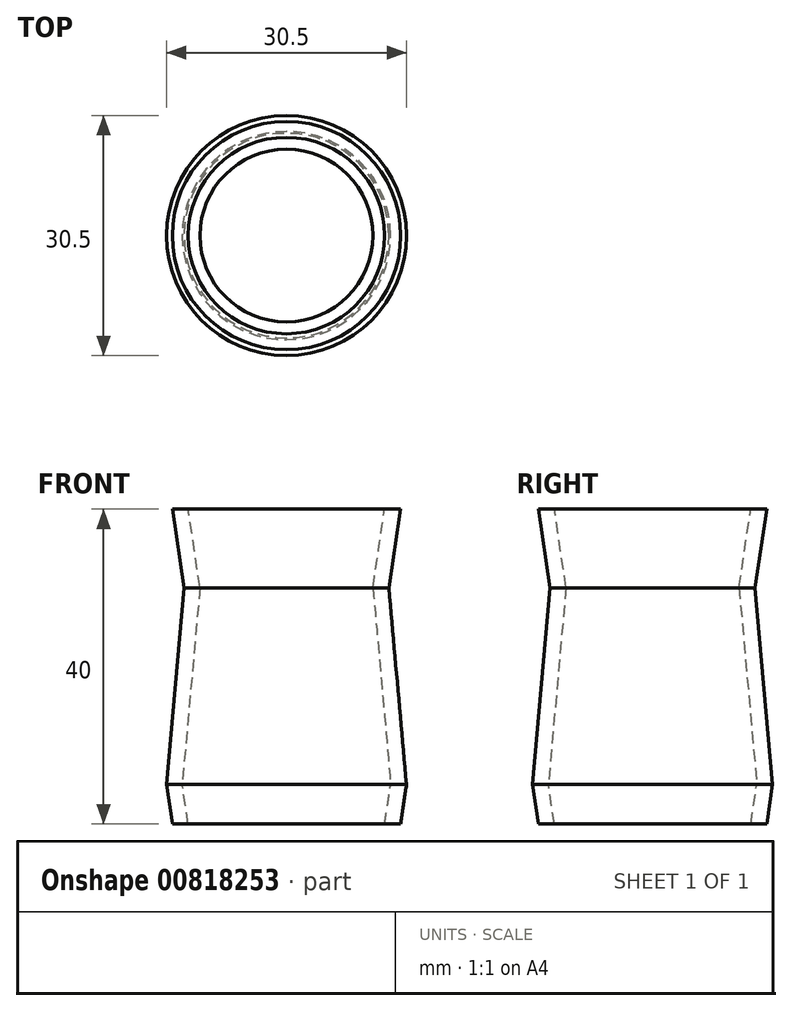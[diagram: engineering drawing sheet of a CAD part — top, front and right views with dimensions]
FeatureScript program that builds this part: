
annotation { "Feature Type Name" : "Feature", "Feature Type Description" : "" }
export const myFeature = defineFeature(function(context is Context, id is Id, definition is map)
    precondition{}
    {
        {
            var Q0;
            Q0=qCreatedBy(makeId("Top.planeOp"),FACE);
            var sketch = newSketch(context, id + "F0", { "sketchPlane" : qUnion([Q0])});
            skCircle(sketch, "E0", {"center": v(0, 0) * mm, "radius": 14.5 * mm});
            skSolve(sketch);
        }
        {
            var Q0;
            Q0=qCreatedBy(makeId("Top.planeOp"),FACE);
            cPlane(context, id + "F1", {"entities" : qUnion([Q0]), "cplaneType" : CPlaneType.OFFSET, "offset" : 5 * mm, "width" : 150 * mm, "height" : 150 * mm});
        }
        {
            var Q0;
            Q0=qCreatedBy(id+"F1.planeOp",FACE);
            var sketch = newSketch(context, id + "F2", { "sketchPlane" : qUnion([Q0])});
            skCircle(sketch, "E1", {"center": v(0, 0) * mm, "radius": 15.25 * mm});
            skSolve(sketch);
        }
        {
            var Q0;
            Q0 = qSketchRegion(id + "F0", true);
            var Q1;
            Q1 = qSketchRegion(id + "F2", true);
            loft(context, id + "F3", {"sheetProfilesArray" : [{ "sheetProfileEntities" : qUnion([Q0]) }, { "sheetProfileEntities" : qUnion([Q1]) }]});
        }
        {
            var Q0;
            Q0=makeQuery(id+"F3.opLoft","CAP_FACE",FACE,{"disambiguationData":[OSD([makeQuery(id+"F2.imprint","IMPRINT",FACE,{"disambiguationData":[TD([[makeQuery(id+"F2.imprint","IMPRINT",EDGE,{"derivedFrom":sQuery(id+"F2.wireOp",EDGE,"E1")}),1.0]])]})])],"isStart":true});
            cPlane(context, id + "F4", {"entities" : qUnion([Q0]), "cplaneType" : CPlaneType.OFFSET, "offset" : 25 * mm, "width" : 150 * mm, "height" : 150 * mm});
        }
        {
            var Q0;
            Q0=qCreatedBy(id+"F4.planeOp",FACE);
            var sketch = newSketch(context, id + "F5", { "sketchPlane" : qUnion([Q0])});
            skCircle(sketch, "E2", {"center": v(0, 0) * mm, "radius": 13 * mm});
            skSolve(sketch);
        }
        {
            var Q1;
            Q1=makeQuery(id+"F3.opLoft","CAP_FACE",FACE,{"disambiguationData":[OSD([makeQuery(id+"F2.imprint","IMPRINT",FACE,{"disambiguationData":[TD([[makeQuery(id+"F2.imprint","IMPRINT",EDGE,{"derivedFrom":sQuery(id+"F2.wireOp",EDGE,"E1")}),1.0]])]})])],"isStart":true});
            var Q2;
            Q2=makeQuery(id+"F5.imprint","IMPRINT",FACE,{"disambiguationData":[TD([[makeQuery(id+"F5.imprint","IMPRINT",EDGE,{"derivedFrom":sQuery(id+"F5.wireOp",EDGE,"E2")}),1.0]])]});
            loft(context, id + "F6", {"operationType" : NewBodyOperationType.ADD, "sheetProfilesArray" : [{ "sheetProfileEntities" : qUnion([Q1]) }, { "sheetProfileEntities" : qUnion([Q2]) }]});
        }
        {
            var Q0;
            Q0=makeQuery(id+"F6.opLoft","CAP_FACE",FACE,{"disambiguationData":[OSD([makeQuery(id+"F5.imprint","IMPRINT",FACE,{"disambiguationData":[TD([[makeQuery(id+"F5.imprint","IMPRINT",EDGE,{"derivedFrom":sQuery(id+"F5.wireOp",EDGE,"E2")}),1.0]])]})])],"isStart":true});
            cPlane(context, id + "F7", {"entities" : qUnion([Q0]), "cplaneType" : CPlaneType.OFFSET, "offset" : 10 * mm, "width" : 150 * mm, "height" : 150 * mm});
        }
        {
            var Q0;
            Q0=qCreatedBy(id+"F7.planeOp",FACE);
            var sketch = newSketch(context, id + "F8", { "sketchPlane" : qUnion([Q0])});
            skCircle(sketch, "E3", {"center": v(0, 0) * mm, "radius": 14.5 * mm});
            skSolve(sketch);
        }
        {
            var Q1;
            Q1=makeQuery(id+"F6.opLoft","CAP_FACE",FACE,{"disambiguationData":[OSD([makeQuery(id+"F5.imprint","IMPRINT",FACE,{"disambiguationData":[TD([[makeQuery(id+"F5.imprint","IMPRINT",EDGE,{"derivedFrom":sQuery(id+"F5.wireOp",EDGE,"E2")}),1.0]])]})])],"isStart":true});
            var Q2;
            Q2=makeQuery(id+"F8.imprint","IMPRINT",FACE,{"disambiguationData":[TD([[makeQuery(id+"F8.imprint","IMPRINT",EDGE,{"derivedFrom":sQuery(id+"F8.wireOp",EDGE,"E3")}),1.0]])]});
            loft(context, id + "F9", {"operationType" : NewBodyOperationType.ADD, "sheetProfilesArray" : [{ "sheetProfileEntities" : qUnion([Q1]) }, { "sheetProfileEntities" : qUnion([Q2]) }]});
        }
        {
            var Q0;
            Q0=makeQuery(id+"F9.opLoft","CAP_FACE",FACE,{"disambiguationData":[OSD([makeQuery(id+"F8.imprint","IMPRINT",FACE,{"disambiguationData":[TD([[makeQuery(id+"F8.imprint","IMPRINT",EDGE,{"derivedFrom":sQuery(id+"F8.wireOp",EDGE,"E3")}),1.0]])]})])],"isStart":true});
            var Q1;
            Q1=makeQuery(id+"F3.opLoft","CAP_FACE",FACE,{"disambiguationData":[OSD([makeQuery(id+"F0.imprint","IMPRINT",FACE,{"disambiguationData":[TD([[makeQuery(id+"F0.imprint","IMPRINT",EDGE,{"derivedFrom":sQuery(id+"F0.wireOp",EDGE,"E0")}),1.0]])]})])],"isStart":true});
            shell(context, id + "F10", {"entities" : qUnion([Q0, Q1]), "thickness" : 2 * mm});
        }
    });
